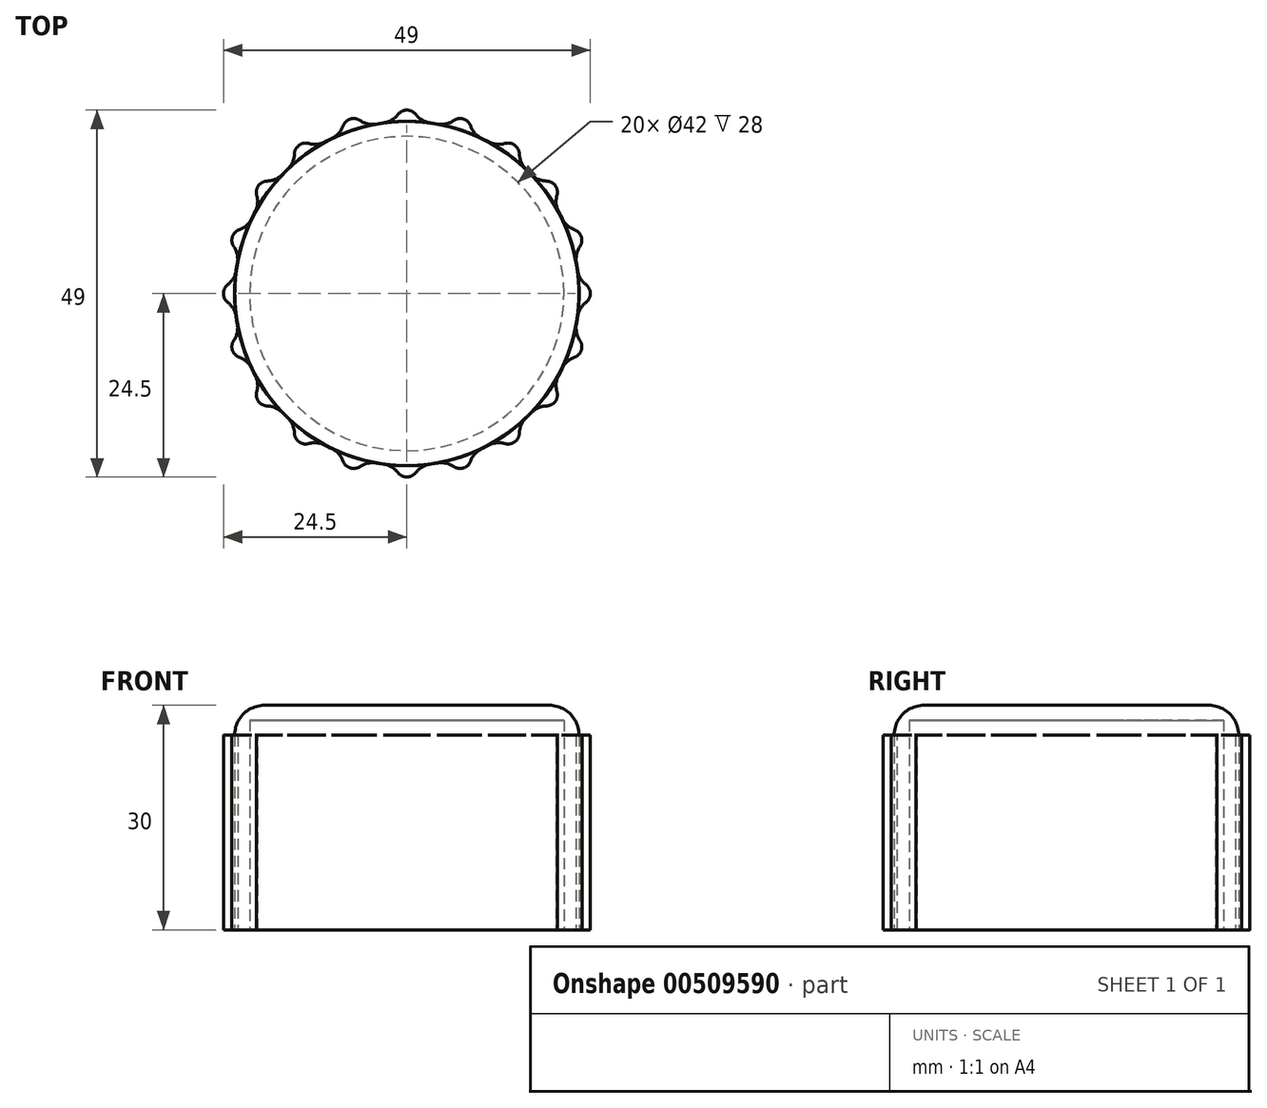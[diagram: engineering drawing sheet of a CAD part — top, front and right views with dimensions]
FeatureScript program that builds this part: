
annotation { "Feature Type Name" : "Feature", "Feature Type Description" : "" }
export const myFeature = defineFeature(function(context is Context, id is Id, definition is map)
    precondition{}
    {
        {
            var Q0;
            Q0=qCreatedBy(makeId("Top.planeOp"),FACE);
            var sketch = newSketch(context, id + "F0", { "sketchPlane" : qUnion([Q0])});
            skCircle(sketch, "E0", {"center": v(0, 0) * mm, "radius": 23 * mm});
            skSolve(sketch);
        }
        {
            var Q0;
            Q0=makeQuery(id+"F0.imprint","IMPRINT",FACE,{"disambiguationData":[TD([[makeQuery(id+"F0.imprint","IMPRINT",EDGE,{"derivedFrom":sQuery(id+"F0.wireOp",EDGE,"E0")}),1.0]])]});
            extrude(context, id + "F1", {"entities" : qUnion([Q0]), "depth" : 30 * mm});
        }
        {
            var Q0;
            Q0=makeQuery(id+"F1.opExtrude","CAP_FACE",FACE,{"disambiguationData":[OSD([sQuery(id+"F0.wireOp",EDGE,"E0")])],"isStart":true});
            shell(context, id + "F2", {"entities" : qUnion([Q0]), "thickness" : 2 * mm});
        }
        {
            var Q0;
            Q0=makeQuery(id+"F1.opExtrude","CAP_EDGE",EDGE,{"disambiguationData":[OSD([sQuery(id+"F0.wireOp",EDGE,"E0")])],"isStart":false});
            fillet(context, id + "F3", {"entities" : qUnion([Q0]), "radius" : 4 * mm, "tangentPropagation" : true, "allowEdgeOverflow" : false});
        }
        {
            var Q0;
            Q0=qCreatedBy(makeId("Top.planeOp"),FACE);
            cPlane(context, id + "F4", {"entities" : qUnion([Q0]), "cplaneType" : CPlaneType.OFFSET, "offset" : 26 * mm, "width" : 150 * mm, "height" : 150 * mm});
        }
        {
            var Q0;
            Q0=qCreatedBy(id+"F4.planeOp",FACE);
            var sketch = newSketch(context, id + "F5", { "sketchPlane" : qUnion([Q0])});
            skCircle(sketch, "E1", {"center": v(-23, 0) * mm, "radius": 1.5 * mm});
            skSolve(sketch);
        }
        {
            var Q0;
            Q0=makeQuery(id+"F5.imprint","IMPRINT",FACE,{"disambiguationData":[TD([[makeQuery(id+"F5.imprint","IMPRINT",EDGE,{"derivedFrom":sQuery(id+"F5.wireOp",EDGE,"E1")}),1.0]])]});
            extrude(context, id + "F6", {"entities" : qUnion([Q0]), "operationType" : NewBodyOperationType.ADD, "oppositeDirection" : true, "depth" : 26 * mm});
        }
        {
            var Q0;
            Q0=makeQuery(id+"F1.opExtrude","SWEPT_BODY",BODY,{"disambiguationData":[OSD([sQuery(id+"F0.wireOp",EDGE,"E0")])]});
            var Q1;
            Q1=makeQuery(id+"F1.opExtrude","SWEPT_FACE",FACE,{"disambiguationData":[OSD([sQuery(id+"F0.wireOp",EDGE,"E0")])]});
            circularPattern(context, id + "F7", {"entities" : qUnion([Q0]), "axis" : qUnion([Q1]), "angle" : 360 * degree, "instanceCount" : 20, "equalSpace" : true});
        }
        {
            var Q0;
            Q0=makeQuery(id+"F7.opPattern","COPY",EDGE,{"derivedFrom":makeQuery(id+"F6.boolean.opBoolean","INTERSECT",EDGE,{"disambiguationData":[OD(1.0)],"derivedFrom":[makeQuery(id+"F1.opExtrude","SWEPT_FACE",FACE,{"disambiguationData":[OSD([sQuery(id+"F0.wireOp",EDGE,"E0")])]}),makeQuery(id+"F6.opExtrude","SWEPT_FACE",FACE,{"disambiguationData":[OSD([sQuery(id+"F5.wireOp",EDGE,"E1")])]})]}),"instanceName":"14"});
            var Q1;
            Q1=makeQuery(id+"F7.opPattern","COPY",EDGE,{"derivedFrom":makeQuery(id+"F6.boolean.opBoolean","INTERSECT",EDGE,{"disambiguationData":[OD(1.0)],"derivedFrom":[makeQuery(id+"F1.opExtrude","SWEPT_FACE",FACE,{"disambiguationData":[OSD([sQuery(id+"F0.wireOp",EDGE,"E0")])]}),makeQuery(id+"F6.opExtrude","SWEPT_FACE",FACE,{"disambiguationData":[OSD([sQuery(id+"F5.wireOp",EDGE,"E1")])]})]}),"instanceName":"13"});
            var Q2;
            Q2=makeQuery(id+"F7.opPattern","COPY",EDGE,{"derivedFrom":makeQuery(id+"F6.boolean.opBoolean","INTERSECT",EDGE,{"disambiguationData":[OD(1.0)],"derivedFrom":[makeQuery(id+"F1.opExtrude","SWEPT_FACE",FACE,{"disambiguationData":[OSD([sQuery(id+"F0.wireOp",EDGE,"E0")])]}),makeQuery(id+"F6.opExtrude","SWEPT_FACE",FACE,{"disambiguationData":[OSD([sQuery(id+"F5.wireOp",EDGE,"E1")])]})]}),"instanceName":"12"});
            var Q3;
            Q3=makeQuery(id+"F7.opPattern","COPY",EDGE,{"derivedFrom":makeQuery(id+"F6.boolean.opBoolean","INTERSECT",EDGE,{"disambiguationData":[OD(1.0)],"derivedFrom":[makeQuery(id+"F1.opExtrude","SWEPT_FACE",FACE,{"disambiguationData":[OSD([sQuery(id+"F0.wireOp",EDGE,"E0")])]}),makeQuery(id+"F6.opExtrude","SWEPT_FACE",FACE,{"disambiguationData":[OSD([sQuery(id+"F5.wireOp",EDGE,"E1")])]})]}),"instanceName":"11"});
            var Q4;
            Q4=makeQuery(id+"F7.opPattern","COPY",EDGE,{"derivedFrom":makeQuery(id+"F6.boolean.opBoolean","INTERSECT",EDGE,{"disambiguationData":[OD(1.0)],"derivedFrom":[makeQuery(id+"F1.opExtrude","SWEPT_FACE",FACE,{"disambiguationData":[OSD([sQuery(id+"F0.wireOp",EDGE,"E0")])]}),makeQuery(id+"F6.opExtrude","SWEPT_FACE",FACE,{"disambiguationData":[OSD([sQuery(id+"F5.wireOp",EDGE,"E1")])]})]}),"instanceName":"10"});
            var Q5;
            Q5=makeQuery(id+"F7.opPattern","COPY",EDGE,{"derivedFrom":makeQuery(id+"F6.boolean.opBoolean","INTERSECT",EDGE,{"disambiguationData":[OD(1.0)],"derivedFrom":[makeQuery(id+"F1.opExtrude","SWEPT_FACE",FACE,{"disambiguationData":[OSD([sQuery(id+"F0.wireOp",EDGE,"E0")])]}),makeQuery(id+"F6.opExtrude","SWEPT_FACE",FACE,{"disambiguationData":[OSD([sQuery(id+"F5.wireOp",EDGE,"E1")])]})]}),"instanceName":"9"});
            var Q6;
            Q6=makeQuery(id+"F7.opPattern","COPY",EDGE,{"derivedFrom":makeQuery(id+"F6.boolean.opBoolean","INTERSECT",EDGE,{"disambiguationData":[OD(0.0)],"derivedFrom":[makeQuery(id+"F1.opExtrude","SWEPT_FACE",FACE,{"disambiguationData":[OSD([sQuery(id+"F0.wireOp",EDGE,"E0")])]}),makeQuery(id+"F6.opExtrude","SWEPT_FACE",FACE,{"disambiguationData":[OSD([sQuery(id+"F5.wireOp",EDGE,"E1")])]})]}),"instanceName":"8"});
            var Q7;
            Q7=makeQuery(id+"F7.opPattern","COPY",EDGE,{"derivedFrom":makeQuery(id+"F6.boolean.opBoolean","INTERSECT",EDGE,{"disambiguationData":[OD(1.0)],"derivedFrom":[makeQuery(id+"F1.opExtrude","SWEPT_FACE",FACE,{"disambiguationData":[OSD([sQuery(id+"F0.wireOp",EDGE,"E0")])]}),makeQuery(id+"F6.opExtrude","SWEPT_FACE",FACE,{"disambiguationData":[OSD([sQuery(id+"F5.wireOp",EDGE,"E1")])]})]}),"instanceName":"8"});
            var Q8;
            Q8=makeQuery(id+"F7.opPattern","COPY",EDGE,{"derivedFrom":makeQuery(id+"F6.boolean.opBoolean","INTERSECT",EDGE,{"disambiguationData":[OD(0.0)],"derivedFrom":[makeQuery(id+"F1.opExtrude","SWEPT_FACE",FACE,{"disambiguationData":[OSD([sQuery(id+"F0.wireOp",EDGE,"E0")])]}),makeQuery(id+"F6.opExtrude","SWEPT_FACE",FACE,{"disambiguationData":[OSD([sQuery(id+"F5.wireOp",EDGE,"E1")])]})]}),"instanceName":"9"});
            var Q9;
            Q9=makeQuery(id+"F7.opPattern","COPY",EDGE,{"derivedFrom":makeQuery(id+"F6.boolean.opBoolean","INTERSECT",EDGE,{"disambiguationData":[OD(0.0)],"derivedFrom":[makeQuery(id+"F1.opExtrude","SWEPT_FACE",FACE,{"disambiguationData":[OSD([sQuery(id+"F0.wireOp",EDGE,"E0")])]}),makeQuery(id+"F6.opExtrude","SWEPT_FACE",FACE,{"disambiguationData":[OSD([sQuery(id+"F5.wireOp",EDGE,"E1")])]})]}),"instanceName":"10"});
            var Q10;
            Q10=makeQuery(id+"F7.opPattern","COPY",EDGE,{"derivedFrom":makeQuery(id+"F6.boolean.opBoolean","INTERSECT",EDGE,{"disambiguationData":[OD(0.0)],"derivedFrom":[makeQuery(id+"F1.opExtrude","SWEPT_FACE",FACE,{"disambiguationData":[OSD([sQuery(id+"F0.wireOp",EDGE,"E0")])]}),makeQuery(id+"F6.opExtrude","SWEPT_FACE",FACE,{"disambiguationData":[OSD([sQuery(id+"F5.wireOp",EDGE,"E1")])]})]}),"instanceName":"11"});
            var Q11;
            Q11=makeQuery(id+"F7.opPattern","COPY",EDGE,{"derivedFrom":makeQuery(id+"F6.boolean.opBoolean","INTERSECT",EDGE,{"disambiguationData":[OD(0.0)],"derivedFrom":[makeQuery(id+"F1.opExtrude","SWEPT_FACE",FACE,{"disambiguationData":[OSD([sQuery(id+"F0.wireOp",EDGE,"E0")])]}),makeQuery(id+"F6.opExtrude","SWEPT_FACE",FACE,{"disambiguationData":[OSD([sQuery(id+"F5.wireOp",EDGE,"E1")])]})]}),"instanceName":"12"});
            var Q12;
            Q12=makeQuery(id+"F7.opPattern","COPY",EDGE,{"derivedFrom":makeQuery(id+"F6.boolean.opBoolean","INTERSECT",EDGE,{"disambiguationData":[OD(0.0)],"derivedFrom":[makeQuery(id+"F1.opExtrude","SWEPT_FACE",FACE,{"disambiguationData":[OSD([sQuery(id+"F0.wireOp",EDGE,"E0")])]}),makeQuery(id+"F6.opExtrude","SWEPT_FACE",FACE,{"disambiguationData":[OSD([sQuery(id+"F5.wireOp",EDGE,"E1")])]})]}),"instanceName":"13"});
            var Q13;
            Q13=makeQuery(id+"F7.opPattern","COPY",EDGE,{"derivedFrom":makeQuery(id+"F6.boolean.opBoolean","INTERSECT",EDGE,{"disambiguationData":[OD(0.0)],"derivedFrom":[makeQuery(id+"F1.opExtrude","SWEPT_FACE",FACE,{"disambiguationData":[OSD([sQuery(id+"F0.wireOp",EDGE,"E0")])]}),makeQuery(id+"F6.opExtrude","SWEPT_FACE",FACE,{"disambiguationData":[OSD([sQuery(id+"F5.wireOp",EDGE,"E1")])]})]}),"instanceName":"14"});
            var Q14;
            Q14=makeQuery(id+"F7.opPattern","COPY",EDGE,{"derivedFrom":makeQuery(id+"F6.boolean.opBoolean","INTERSECT",EDGE,{"disambiguationData":[OD(0.0)],"derivedFrom":[makeQuery(id+"F1.opExtrude","SWEPT_FACE",FACE,{"disambiguationData":[OSD([sQuery(id+"F0.wireOp",EDGE,"E0")])]}),makeQuery(id+"F6.opExtrude","SWEPT_FACE",FACE,{"disambiguationData":[OSD([sQuery(id+"F5.wireOp",EDGE,"E1")])]})]}),"instanceName":"15"});
            var Q15;
            Q15=makeQuery(id+"F7.opPattern","COPY",EDGE,{"derivedFrom":makeQuery(id+"F6.boolean.opBoolean","INTERSECT",EDGE,{"disambiguationData":[OD(0.0)],"derivedFrom":[makeQuery(id+"F1.opExtrude","SWEPT_FACE",FACE,{"disambiguationData":[OSD([sQuery(id+"F0.wireOp",EDGE,"E0")])]}),makeQuery(id+"F6.opExtrude","SWEPT_FACE",FACE,{"disambiguationData":[OSD([sQuery(id+"F5.wireOp",EDGE,"E1")])]})]}),"instanceName":"16"});
            var Q16;
            Q16=makeQuery(id+"F7.opPattern","COPY",EDGE,{"derivedFrom":makeQuery(id+"F6.boolean.opBoolean","INTERSECT",EDGE,{"disambiguationData":[OD(0.0)],"derivedFrom":[makeQuery(id+"F1.opExtrude","SWEPT_FACE",FACE,{"disambiguationData":[OSD([sQuery(id+"F0.wireOp",EDGE,"E0")])]}),makeQuery(id+"F6.opExtrude","SWEPT_FACE",FACE,{"disambiguationData":[OSD([sQuery(id+"F5.wireOp",EDGE,"E1")])]})]}),"instanceName":"17"});
            var Q17;
            Q17=makeQuery(id+"F7.opPattern","COPY",EDGE,{"derivedFrom":makeQuery(id+"F6.boolean.opBoolean","INTERSECT",EDGE,{"disambiguationData":[OD(0.0)],"derivedFrom":[makeQuery(id+"F1.opExtrude","SWEPT_FACE",FACE,{"disambiguationData":[OSD([sQuery(id+"F0.wireOp",EDGE,"E0")])]}),makeQuery(id+"F6.opExtrude","SWEPT_FACE",FACE,{"disambiguationData":[OSD([sQuery(id+"F5.wireOp",EDGE,"E1")])]})]}),"instanceName":"18"});
            var Q18;
            Q18=makeQuery(id+"F7.opPattern","COPY",EDGE,{"derivedFrom":makeQuery(id+"F6.boolean.opBoolean","INTERSECT",EDGE,{"disambiguationData":[OD(0.0)],"derivedFrom":[makeQuery(id+"F1.opExtrude","SWEPT_FACE",FACE,{"disambiguationData":[OSD([sQuery(id+"F0.wireOp",EDGE,"E0")])]}),makeQuery(id+"F6.opExtrude","SWEPT_FACE",FACE,{"disambiguationData":[OSD([sQuery(id+"F5.wireOp",EDGE,"E1")])]})]}),"instanceName":"19"});
            var Q19;
            Q19=makeQuery(id+"F6.boolean.opBoolean","INTERSECT",EDGE,{"disambiguationData":[OD(0.0)],"derivedFrom":[makeQuery(id+"F1.opExtrude","SWEPT_FACE",FACE,{"disambiguationData":[OSD([sQuery(id+"F0.wireOp",EDGE,"E0")])]}),makeQuery(id+"F6.opExtrude","SWEPT_FACE",FACE,{"disambiguationData":[OSD([sQuery(id+"F5.wireOp",EDGE,"E1")])]})]});
            var Q20;
            Q20=makeQuery(id+"F7.opPattern","COPY",EDGE,{"derivedFrom":makeQuery(id+"F6.boolean.opBoolean","INTERSECT",EDGE,{"disambiguationData":[OD(1.0)],"derivedFrom":[makeQuery(id+"F1.opExtrude","SWEPT_FACE",FACE,{"disambiguationData":[OSD([sQuery(id+"F0.wireOp",EDGE,"E0")])]}),makeQuery(id+"F6.opExtrude","SWEPT_FACE",FACE,{"disambiguationData":[OSD([sQuery(id+"F5.wireOp",EDGE,"E1")])]})]}),"instanceName":"15"});
            var Q21;
            Q21=makeQuery(id+"F7.opPattern","COPY",EDGE,{"derivedFrom":makeQuery(id+"F6.boolean.opBoolean","INTERSECT",EDGE,{"disambiguationData":[OD(1.0)],"derivedFrom":[makeQuery(id+"F1.opExtrude","SWEPT_FACE",FACE,{"disambiguationData":[OSD([sQuery(id+"F0.wireOp",EDGE,"E0")])]}),makeQuery(id+"F6.opExtrude","SWEPT_FACE",FACE,{"disambiguationData":[OSD([sQuery(id+"F5.wireOp",EDGE,"E1")])]})]}),"instanceName":"16"});
            var Q22;
            Q22=makeQuery(id+"F7.opPattern","COPY",EDGE,{"derivedFrom":makeQuery(id+"F6.boolean.opBoolean","INTERSECT",EDGE,{"disambiguationData":[OD(1.0)],"derivedFrom":[makeQuery(id+"F1.opExtrude","SWEPT_FACE",FACE,{"disambiguationData":[OSD([sQuery(id+"F0.wireOp",EDGE,"E0")])]}),makeQuery(id+"F6.opExtrude","SWEPT_FACE",FACE,{"disambiguationData":[OSD([sQuery(id+"F5.wireOp",EDGE,"E1")])]})]}),"instanceName":"17"});
            var Q23;
            Q23=makeQuery(id+"F7.opPattern","COPY",EDGE,{"derivedFrom":makeQuery(id+"F6.boolean.opBoolean","INTERSECT",EDGE,{"disambiguationData":[OD(1.0)],"derivedFrom":[makeQuery(id+"F1.opExtrude","SWEPT_FACE",FACE,{"disambiguationData":[OSD([sQuery(id+"F0.wireOp",EDGE,"E0")])]}),makeQuery(id+"F6.opExtrude","SWEPT_FACE",FACE,{"disambiguationData":[OSD([sQuery(id+"F5.wireOp",EDGE,"E1")])]})]}),"instanceName":"18"});
            var Q24;
            Q24=makeQuery(id+"F7.opPattern","COPY",EDGE,{"derivedFrom":makeQuery(id+"F6.boolean.opBoolean","INTERSECT",EDGE,{"disambiguationData":[OD(1.0)],"derivedFrom":[makeQuery(id+"F1.opExtrude","SWEPT_FACE",FACE,{"disambiguationData":[OSD([sQuery(id+"F0.wireOp",EDGE,"E0")])]}),makeQuery(id+"F6.opExtrude","SWEPT_FACE",FACE,{"disambiguationData":[OSD([sQuery(id+"F5.wireOp",EDGE,"E1")])]})]}),"instanceName":"19"});
            var Q25;
            Q25=makeQuery(id+"F6.boolean.opBoolean","INTERSECT",EDGE,{"disambiguationData":[OD(1.0)],"derivedFrom":[makeQuery(id+"F1.opExtrude","SWEPT_FACE",FACE,{"disambiguationData":[OSD([sQuery(id+"F0.wireOp",EDGE,"E0")])]}),makeQuery(id+"F6.opExtrude","SWEPT_FACE",FACE,{"disambiguationData":[OSD([sQuery(id+"F5.wireOp",EDGE,"E1")])]})]});
            var Q26;
            Q26=makeQuery(id+"F7.opPattern","COPY",EDGE,{"derivedFrom":makeQuery(id+"F6.boolean.opBoolean","INTERSECT",EDGE,{"disambiguationData":[OD(0.0)],"derivedFrom":[makeQuery(id+"F1.opExtrude","SWEPT_FACE",FACE,{"disambiguationData":[OSD([sQuery(id+"F0.wireOp",EDGE,"E0")])]}),makeQuery(id+"F6.opExtrude","SWEPT_FACE",FACE,{"disambiguationData":[OSD([sQuery(id+"F5.wireOp",EDGE,"E1")])]})]}),"instanceName":"1"});
            var Q27;
            Q27=makeQuery(id+"F7.opPattern","COPY",EDGE,{"derivedFrom":makeQuery(id+"F6.boolean.opBoolean","INTERSECT",EDGE,{"disambiguationData":[OD(1.0)],"derivedFrom":[makeQuery(id+"F1.opExtrude","SWEPT_FACE",FACE,{"disambiguationData":[OSD([sQuery(id+"F0.wireOp",EDGE,"E0")])]}),makeQuery(id+"F6.opExtrude","SWEPT_FACE",FACE,{"disambiguationData":[OSD([sQuery(id+"F5.wireOp",EDGE,"E1")])]})]}),"instanceName":"1"});
            var Q28;
            Q28=makeQuery(id+"F7.opPattern","COPY",EDGE,{"derivedFrom":makeQuery(id+"F6.boolean.opBoolean","INTERSECT",EDGE,{"disambiguationData":[OD(0.0)],"derivedFrom":[makeQuery(id+"F1.opExtrude","SWEPT_FACE",FACE,{"disambiguationData":[OSD([sQuery(id+"F0.wireOp",EDGE,"E0")])]}),makeQuery(id+"F6.opExtrude","SWEPT_FACE",FACE,{"disambiguationData":[OSD([sQuery(id+"F5.wireOp",EDGE,"E1")])]})]}),"instanceName":"2"});
            var Q29;
            Q29=makeQuery(id+"F7.opPattern","COPY",EDGE,{"derivedFrom":makeQuery(id+"F6.boolean.opBoolean","INTERSECT",EDGE,{"disambiguationData":[OD(1.0)],"derivedFrom":[makeQuery(id+"F1.opExtrude","SWEPT_FACE",FACE,{"disambiguationData":[OSD([sQuery(id+"F0.wireOp",EDGE,"E0")])]}),makeQuery(id+"F6.opExtrude","SWEPT_FACE",FACE,{"disambiguationData":[OSD([sQuery(id+"F5.wireOp",EDGE,"E1")])]})]}),"instanceName":"2"});
            var Q30;
            Q30=makeQuery(id+"F7.opPattern","COPY",EDGE,{"derivedFrom":makeQuery(id+"F6.boolean.opBoolean","INTERSECT",EDGE,{"disambiguationData":[OD(1.0)],"derivedFrom":[makeQuery(id+"F1.opExtrude","SWEPT_FACE",FACE,{"disambiguationData":[OSD([sQuery(id+"F0.wireOp",EDGE,"E0")])]}),makeQuery(id+"F6.opExtrude","SWEPT_FACE",FACE,{"disambiguationData":[OSD([sQuery(id+"F5.wireOp",EDGE,"E1")])]})]}),"instanceName":"3"});
            var Q31;
            Q31=makeQuery(id+"F7.opPattern","COPY",EDGE,{"derivedFrom":makeQuery(id+"F6.boolean.opBoolean","INTERSECT",EDGE,{"disambiguationData":[OD(0.0)],"derivedFrom":[makeQuery(id+"F1.opExtrude","SWEPT_FACE",FACE,{"disambiguationData":[OSD([sQuery(id+"F0.wireOp",EDGE,"E0")])]}),makeQuery(id+"F6.opExtrude","SWEPT_FACE",FACE,{"disambiguationData":[OSD([sQuery(id+"F5.wireOp",EDGE,"E1")])]})]}),"instanceName":"3"});
            var Q32;
            Q32=makeQuery(id+"F7.opPattern","COPY",EDGE,{"derivedFrom":makeQuery(id+"F6.boolean.opBoolean","INTERSECT",EDGE,{"disambiguationData":[OD(0.0)],"derivedFrom":[makeQuery(id+"F1.opExtrude","SWEPT_FACE",FACE,{"disambiguationData":[OSD([sQuery(id+"F0.wireOp",EDGE,"E0")])]}),makeQuery(id+"F6.opExtrude","SWEPT_FACE",FACE,{"disambiguationData":[OSD([sQuery(id+"F5.wireOp",EDGE,"E1")])]})]}),"instanceName":"4"});
            var Q33;
            Q33=makeQuery(id+"F7.opPattern","COPY",EDGE,{"derivedFrom":makeQuery(id+"F6.boolean.opBoolean","INTERSECT",EDGE,{"disambiguationData":[OD(0.0)],"derivedFrom":[makeQuery(id+"F1.opExtrude","SWEPT_FACE",FACE,{"disambiguationData":[OSD([sQuery(id+"F0.wireOp",EDGE,"E0")])]}),makeQuery(id+"F6.opExtrude","SWEPT_FACE",FACE,{"disambiguationData":[OSD([sQuery(id+"F5.wireOp",EDGE,"E1")])]})]}),"instanceName":"5"});
            var Q34;
            Q34=makeQuery(id+"F7.opPattern","COPY",EDGE,{"derivedFrom":makeQuery(id+"F6.boolean.opBoolean","INTERSECT",EDGE,{"disambiguationData":[OD(1.0)],"derivedFrom":[makeQuery(id+"F1.opExtrude","SWEPT_FACE",FACE,{"disambiguationData":[OSD([sQuery(id+"F0.wireOp",EDGE,"E0")])]}),makeQuery(id+"F6.opExtrude","SWEPT_FACE",FACE,{"disambiguationData":[OSD([sQuery(id+"F5.wireOp",EDGE,"E1")])]})]}),"instanceName":"4"});
            var Q35;
            Q35=makeQuery(id+"F7.opPattern","COPY",EDGE,{"derivedFrom":makeQuery(id+"F6.boolean.opBoolean","INTERSECT",EDGE,{"disambiguationData":[OD(0.0)],"derivedFrom":[makeQuery(id+"F1.opExtrude","SWEPT_FACE",FACE,{"disambiguationData":[OSD([sQuery(id+"F0.wireOp",EDGE,"E0")])]}),makeQuery(id+"F6.opExtrude","SWEPT_FACE",FACE,{"disambiguationData":[OSD([sQuery(id+"F5.wireOp",EDGE,"E1")])]})]}),"instanceName":"6"});
            var Q36;
            Q36=makeQuery(id+"F7.opPattern","COPY",EDGE,{"derivedFrom":makeQuery(id+"F6.boolean.opBoolean","INTERSECT",EDGE,{"disambiguationData":[OD(0.0)],"derivedFrom":[makeQuery(id+"F1.opExtrude","SWEPT_FACE",FACE,{"disambiguationData":[OSD([sQuery(id+"F0.wireOp",EDGE,"E0")])]}),makeQuery(id+"F6.opExtrude","SWEPT_FACE",FACE,{"disambiguationData":[OSD([sQuery(id+"F5.wireOp",EDGE,"E1")])]})]}),"instanceName":"7"});
            var Q37;
            Q37=makeQuery(id+"F7.opPattern","COPY",EDGE,{"derivedFrom":makeQuery(id+"F6.boolean.opBoolean","INTERSECT",EDGE,{"disambiguationData":[OD(1.0)],"derivedFrom":[makeQuery(id+"F1.opExtrude","SWEPT_FACE",FACE,{"disambiguationData":[OSD([sQuery(id+"F0.wireOp",EDGE,"E0")])]}),makeQuery(id+"F6.opExtrude","SWEPT_FACE",FACE,{"disambiguationData":[OSD([sQuery(id+"F5.wireOp",EDGE,"E1")])]})]}),"instanceName":"5"});
            var Q38;
            Q38=makeQuery(id+"F7.opPattern","COPY",EDGE,{"derivedFrom":makeQuery(id+"F6.boolean.opBoolean","INTERSECT",EDGE,{"disambiguationData":[OD(1.0)],"derivedFrom":[makeQuery(id+"F1.opExtrude","SWEPT_FACE",FACE,{"disambiguationData":[OSD([sQuery(id+"F0.wireOp",EDGE,"E0")])]}),makeQuery(id+"F6.opExtrude","SWEPT_FACE",FACE,{"disambiguationData":[OSD([sQuery(id+"F5.wireOp",EDGE,"E1")])]})]}),"instanceName":"6"});
            var Q39;
            Q39=makeQuery(id+"F7.opPattern","COPY",EDGE,{"derivedFrom":makeQuery(id+"F6.boolean.opBoolean","INTERSECT",EDGE,{"disambiguationData":[OD(1.0)],"derivedFrom":[makeQuery(id+"F1.opExtrude","SWEPT_FACE",FACE,{"disambiguationData":[OSD([sQuery(id+"F0.wireOp",EDGE,"E0")])]}),makeQuery(id+"F6.opExtrude","SWEPT_FACE",FACE,{"disambiguationData":[OSD([sQuery(id+"F5.wireOp",EDGE,"E1")])]})]}),"instanceName":"7"});
            fillet(context, id + "F8", {"entities" : qUnion([Q0, Q1, Q2, Q3, Q4, Q5, Q6, Q7, Q8, Q9, Q10, Q11, Q12, Q13, Q14, Q15, Q16, Q17, Q18, Q19, Q20, Q21, Q22, Q23, Q24, Q25, Q26, Q27, Q28, Q29, Q30, Q31, Q32, Q33, Q34, Q35, Q36, Q37, Q38, Q39]), "radius" : 3 * mm, "tangentPropagation" : true, "allowEdgeOverflow" : false});
        }
    });
